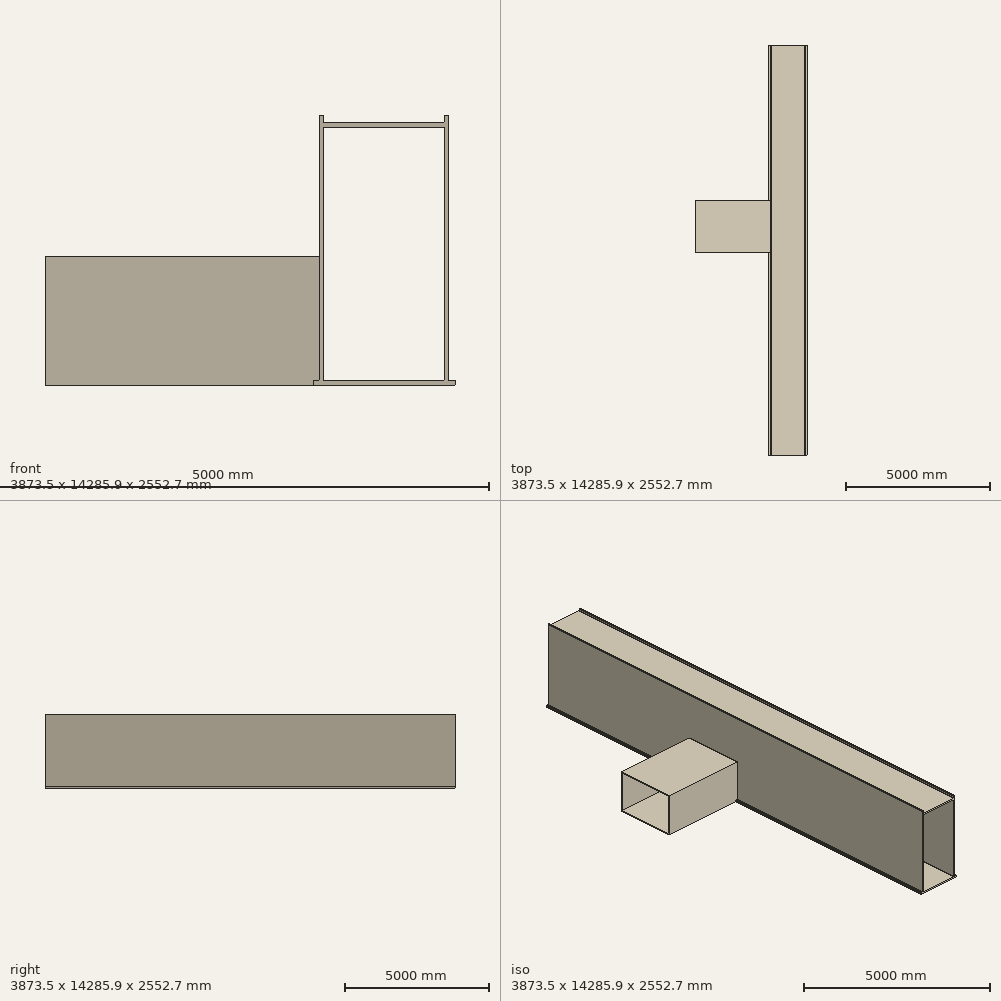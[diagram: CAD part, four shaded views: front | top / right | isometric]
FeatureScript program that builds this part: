
annotation { "Feature Type Name" : "Feature", "Feature Type Description" : "" }
export const myFeature = defineFeature(function(context is Context, id is Id, definition is map)
    precondition{}
    {
        {
            var Q0;
            Q0=qCreatedBy(makeId("Front.planeOp"),FACE);
            var sketch = newSketch(context, id + "F0", { "sketchPlane" : qUnion([Q0])});
            skLineSegment(sketch, "E0.bottom", {"start": v(710, -1271.59) * mm, "end": v(-636.2, -1271.59) * mm});
            skLineSegment(sketch, "E0.top", {"start": v(710, -1220.79) * mm, "end": v(-636.2, -1220.79) * mm});
            skLineSegment(sketch, "E0.left", {"start": v(710, -1271.59) * mm, "end": v(710, -1220.79) * mm});
            skLineSegment(sketch, "E0.right", {"start": v(-636.2, -1271.59) * mm, "end": v(-636.2, -1220.79) * mm});
            skPoint(sketch, "E0.middle", {"position": v(36.9, -1246.19) * mm});
            skLineSegment(sketch, "E1.bottom", {"start": v(-534.6, -1220.79) * mm, "end": v(-572.7, -1220.79) * mm});
            skLineSegment(sketch, "E1.top", {"start": v(-534.6, 1281.11) * mm, "end": v(-572.7, 1281.11) * mm});
            skLineSegment(sketch, "E1.left", {"start": v(-534.6, -1220.79) * mm, "end": v(-534.6, 1281.11) * mm});
            skLineSegment(sketch, "E1.right", {"start": v(-572.7, -1220.79) * mm, "end": v(-572.7, 1281.11) * mm});
            skLineSegment(sketch, "E2.MirrorCS", {"start": v(608.4, 1281.11) * mm, "end": v(646.5, 1281.11) * mm});
            skLineSegment(sketch, "E3.MirrorCS", {"start": v(646.5, -1220.79) * mm, "end": v(646.5, 1281.11) * mm});
            skLineSegment(sketch, "E4.MirrorCS", {"start": v(608.4, -1220.79) * mm, "end": v(608.4, 1281.11) * mm});
            skLineSegment(sketch, "E5.bottom", {"start": v(-534.6, 1217.61) * mm, "end": v(608.4, 1217.61) * mm});
            skLineSegment(sketch, "E5.top", {"start": v(-534.6, 1166.81) * mm, "end": v(608.4, 1166.81) * mm});
            skLineSegment(sketch, "E5.left", {"start": v(-534.6, 1217.61) * mm, "end": v(-534.6, 1166.81) * mm});
            skLineSegment(sketch, "E5.right", {"start": v(608.4, 1217.61) * mm, "end": v(608.4, 1166.81) * mm});
            skSolve(sketch);
        }
        {
            var Q0;
            Q0 = qSketchRegion(id + "F0", true);
            extrude(context, id + "F1", {"entities" : qUnion([Q0]), "depth" : 14285.91 * mm});
        }
        {
            var Q0;
            Q0=makeQuery(id+"F1.opExtrude","SWEPT_FACE",FACE,{"disambiguationData":[OSD([sQuery(id+"F0.wireOp",EDGE,"E0.right")])]});
            var sketch = newSketch(context, id + "F2", { "sketchPlane" : qUnion([Q0])});
            skLineSegment(sketch, "E6.bottom", {"start": v(5384.8, -1271.59) * mm, "end": v(7213.6, -1271.59) * mm});
            skLineSegment(sketch, "E6.top", {"start": v(5384.8, -52.39) * mm, "end": v(7213.6, -52.39) * mm});
            skLineSegment(sketch, "E6.left", {"start": v(5384.8, -1271.59) * mm, "end": v(5384.8, -52.39) * mm});
            skLineSegment(sketch, "E6.right", {"start": v(7213.6, -1271.59) * mm, "end": v(7213.6, -52.39) * mm});
            skLineSegment(sketch, "E7", {"start": v(7188.2, -1252.54) * mm, "end": v(7188.2, -71.44) * mm});
            skLineSegment(sketch, "E8", {"start": v(5410.2, -1252.54) * mm, "end": v(5410.2, -71.44) * mm});
            skLineSegment(sketch, "E9", {"start": v(7188.2, -71.44) * mm, "end": v(5410.2, -71.44) * mm});
            skLineSegment(sketch, "E10", {"start": v(7188.2, -1252.54) * mm, "end": v(5410.2, -1252.54) * mm});
            skSolve(sketch);
        }
        {
            var Q0;
            Q0 = qSketchRegion(id + "F2", true);
            extrude(context, id + "F3", {"entities" : qUnion([Q0]), "operationType" : NewBodyOperationType.ADD, "depth" : 2527.3 * mm, "hasSecondDirection" : true, "secondDirectionOppositeDirection" : true, "secondDirectionDepth" : 63.5 * mm});
        }
    });
